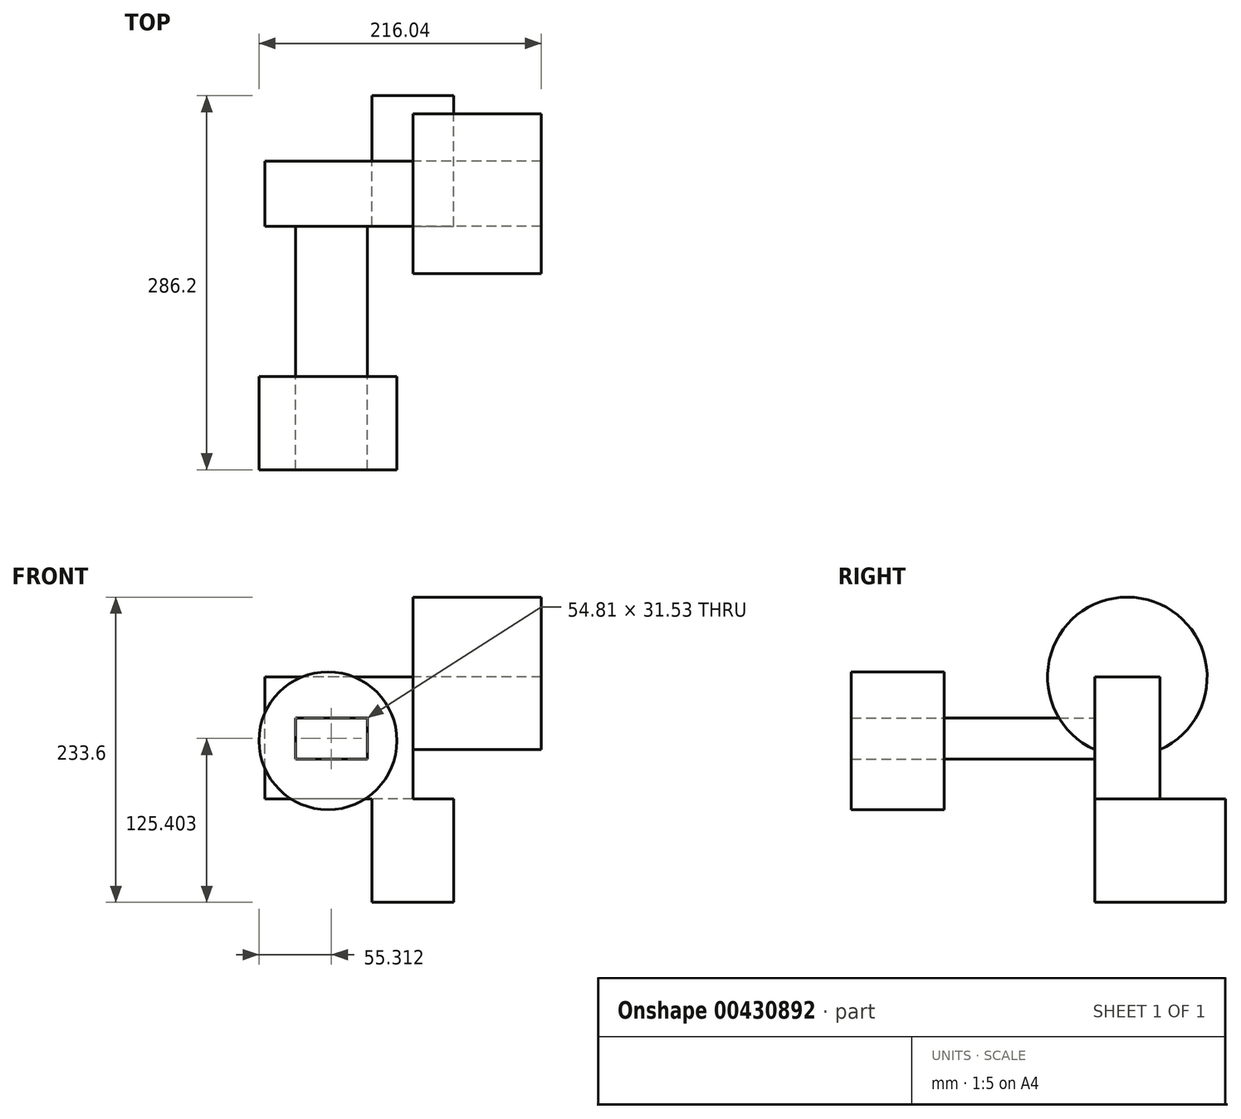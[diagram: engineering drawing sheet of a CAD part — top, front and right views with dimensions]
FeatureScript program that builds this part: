
annotation { "Feature Type Name" : "Feature", "Feature Type Description" : "" }
export const myFeature = defineFeature(function(context is Context, id is Id, definition is map)
    precondition{}
    {
        {
            var Q0;
            Q0=qCreatedBy(makeId("Front.planeOp"),FACE);
            var sketch = newSketch(context, id + "F0", { "sketchPlane" : qUnion([Q0])});
            skLineSegment(sketch, "E0.bottom", {"start": v(56.63, -46.67) * mm, "end": v(-56.63, -46.67) * mm});
            skLineSegment(sketch, "E0.top", {"start": v(56.63, 46.67) * mm, "end": v(-56.63, 46.67) * mm});
            skLineSegment(sketch, "E0.left", {"start": v(56.63, -46.67) * mm, "end": v(56.63, 46.67) * mm});
            skLineSegment(sketch, "E0.right", {"start": v(-56.63, -46.67) * mm, "end": v(-56.63, 46.67) * mm});
            skPoint(sketch, "E0.middle", {"position": v(0, 0) * mm});
            skSolve(sketch);
        }
        {
            var Q0;
            Q0=makeQuery(id+"F0.imprint","IMPRINT",FACE,{"disambiguationData":[TD([[makeQuery(id+"F0.imprint","IMPRINT",EDGE,{"derivedFrom":sQuery(id+"F0.wireOp",EDGE,"E0.bottom")}),-1.0]])]});
            extrude(context, id + "F1", {"entities" : qUnion([Q0]), "depth" : 25 * mm});
        }
        {
            var Q0;
            Q0=makeQuery(id+"F1.opExtrude","CAP_FACE",FACE,{"disambiguationData":[OSD([sQuery(id+"F0.wireOp",EDGE,"E0.bottom"),sQuery(id+"F0.wireOp",EDGE,"E0.top"),sQuery(id+"F0.wireOp",EDGE,"E0.left"),sQuery(id+"F0.wireOp",EDGE,"E0.right")])],"isStart":false});
            var sketch = newSketch(context, id + "F2", { "sketchPlane" : qUnion([Q0])});
            skLineSegment(sketch, "E1.bottom", {"start": v(21.62, -16.23) * mm, "end": v(-33.18, -16.23) * mm});
            skLineSegment(sketch, "E1.top", {"start": v(21.62, 15.3) * mm, "end": v(-33.18, 15.3) * mm});
            skLineSegment(sketch, "E1.left", {"start": v(21.62, -16.23) * mm, "end": v(21.62, 15.3) * mm});
            skLineSegment(sketch, "E1.right", {"start": v(-33.18, -16.23) * mm, "end": v(-33.18, 15.3) * mm});
            skSolve(sketch);
        }
        {
            var Q0;
            Q0=makeQuery(id+"F2.imprint","IMPRINT",FACE,{"disambiguationData":[TD([[makeQuery(id+"F2.imprint","IMPRINT",EDGE,{"derivedFrom":sQuery(id+"F2.wireOp",EDGE,"E1.bottom")}),-1.0]])]});
            extrude(context, id + "F3", {"entities" : qUnion([Q0]), "operationType" : NewBodyOperationType.ADD, "depth" : 115.04 * mm});
        }
        {
            var Q0;
            Q0=makeQuery(id+"F3.opExtrude","CAP_FACE",FACE,{"disambiguationData":[OSD([sQuery(id+"F2.wireOp",EDGE,"E1.bottom"),sQuery(id+"F2.wireOp",EDGE,"E1.top"),sQuery(id+"F2.wireOp",EDGE,"E1.left"),sQuery(id+"F2.wireOp",EDGE,"E1.right")])],"isStart":false});
            var sketch = newSketch(context, id + "F4", { "sketchPlane" : qUnion([Q0])});
            skSolve(sketch);
        }
        {
            var Q0;
            Q0=makeQuery(id+"F1.opExtrude","CAP_FACE",FACE,{"disambiguationData":[OSD([sQuery(id+"F0.wireOp",EDGE,"E0.bottom"),sQuery(id+"F0.wireOp",EDGE,"E0.top"),sQuery(id+"F0.wireOp",EDGE,"E0.left"),sQuery(id+"F0.wireOp",EDGE,"E0.right")])],"isStart":false});
            var Q1;
            Q1=makeQuery(id+"F4.imprint","IMPRINT",FACE,{"disambiguationData":[TD([[makeQuery(id+"F4.imprint","IMPRINT",EDGE,{"derivedFrom":makeQuery(id+"F3.opExtrude","CAP_EDGE",EDGE,{"disambiguationData":[OSD([sQuery(id+"F2.wireOp",EDGE,"E1.bottom")])],"isStart":false})}),-1.0]])]});
            extrude(context, id + "F5", {"entities" : qUnion([Q0, Q1]), "operationType" : NewBodyOperationType.ADD, "depth" : 25 * mm});
        }
        {
            var Q0;
            Q0=makeQuery(id+"F5.opExtrude","CAP_FACE",FACE,{"disambiguationData":[OSD([sQuery(id+"F2.wireOp",EDGE,"E1.bottom"),sQuery(id+"F2.wireOp",EDGE,"E1.top"),sQuery(id+"F2.wireOp",EDGE,"E1.left"),sQuery(id+"F2.wireOp",EDGE,"E1.right")])],"isStart":false});
            var sketch = newSketch(context, id + "F6", { "sketchPlane" : qUnion([Q0])});
            skCircle(sketch, "E2", {"center": v(-8.33, -2.19) * mm, "radius": 52.76 * mm});
            skSolve(sketch);
        }
        {
            var Q0;
            Q0=makeQuery(id+"F6.imprint","IMPRINT",FACE,{"disambiguationData":[TD([[makeQuery(id+"F6.imprint","IMPRINT",EDGE,{"derivedFrom":sQuery(id+"F6.wireOp",EDGE,"E2")}),1.0]])]});
            extrude(context, id + "F7", {"entities" : qUnion([Q0]), "depth" : 71.16 * mm});
        }
        {
            var Q0;
            {var subQ0=sQuery(id+"F0.wireOp",EDGE,"E0.bottom");Q0=makeQuery(id+"F5.boolean.opBoolean","MERGE",FACE,{"derivedFrom":[makeQuery(id+"F1.opExtrude","SWEPT_FACE",FACE,{"disambiguationData":[OSD([subQ0])]}),makeQuery(id+"F5.opExtrude","SWEPT_FACE",FACE,{"disambiguationData":[OSD([subQ0])]})]});}
            var sketch = newSketch(context, id + "F8", { "sketchPlane" : qUnion([Q0])});
            skLineSegment(sketch, "E3.bottom", {"start": v(25.33, 50) * mm, "end": v(87.93, 50) * mm});
            skLineSegment(sketch, "E3.top", {"start": v(25.33, -50) * mm, "end": v(87.93, -50) * mm});
            skLineSegment(sketch, "E3.left", {"start": v(25.33, 50) * mm, "end": v(25.33, -50) * mm});
            skLineSegment(sketch, "E3.right", {"start": v(87.93, 50) * mm, "end": v(87.93, -50) * mm});
            skPoint(sketch, "E3.middle", {"position": v(56.63, 0) * mm});
            skSolve(sketch);
        }
        {
            var Q0;
            Q0 = qSketchRegion(id + "F8", true);
            extrude(context, id + "F9", {"entities" : qUnion([Q0]), "operationType" : NewBodyOperationType.ADD, "depth" : 79.2 * mm});
        }
        {
            var Q0;
            Q0=makeQuery(id+"F9.boolean.opBoolean","MERGE",FACE,{"derivedFrom":[makeQuery(id+"F5.opExtrude","CAP_FACE",FACE,{"disambiguationData":[OSD([sQuery(id+"F0.wireOp",EDGE,"E0.bottom"),sQuery(id+"F0.wireOp",EDGE,"E0.top"),sQuery(id+"F0.wireOp",EDGE,"E0.left"),sQuery(id+"F0.wireOp",EDGE,"E0.right")])],"isStart":false}),makeQuery(id+"F9.opExtrude","SWEPT_FACE",FACE,{"disambiguationData":[OSD([sQuery(id+"F8.wireOp",EDGE,"E3.bottom")])]})]});
            var sketch = newSketch(context, id + "F10", { "sketchPlane" : qUnion([Q0])});
            skSolve(sketch);
        }
        {
            var Q0;
            Q0=makeQuery(id+"F10.imprint","IMPRINT",FACE,{"disambiguationData":[TD([[makeQuery(id+"F10.imprint","IMPRINT",EDGE,{"derivedFrom":makeQuery(id+"F5.opExtrude","CAP_EDGE",EDGE,{"disambiguationData":[OSD([sQuery(id+"F0.wireOp",EDGE,"E0.top")])],"isStart":false})}),1.0]])]});
            var sketch = newSketch(context, id + "F11", { "sketchPlane" : qUnion([Q0])});
            skEllipse(sketch, "E4", {"center": v(58.46, -81.77) * mm, "majorRadius": 30.53 * mm, "minorRadius": 60.92 * mm, "majorAxis": v(0, 1)});
            skSolve(sketch);
        }
        {
            var Q0;
            Q0=sQuery(id+"F11.wireOp",EDGE,"E4");
            extrude(context, id + "F12", {"bodyType" : ToolBodyType.SURFACE, "surfaceEntities" : qUnion([Q0]), "depth" : 120.61 * mm});
        }
        {
            var Q0;
            {var subQ0=sQuery(id+"F0.wireOp",EDGE,"E0.left");Q0=makeQuery(id+"F5.boolean.opBoolean","MERGE",FACE,{"derivedFrom":[makeQuery(id+"F1.opExtrude","SWEPT_FACE",FACE,{"disambiguationData":[OSD([subQ0])]}),makeQuery(id+"F5.opExtrude","SWEPT_FACE",FACE,{"disambiguationData":[OSD([subQ0])]})]});}
            var sketch = newSketch(context, id + "F13", { "sketchPlane" : qUnion([Q0])});
            skCircle(sketch, "E5", {"center": v(-25, 46.67) * mm, "radius": 61.05 * mm});
            skSolve(sketch);
        }
        {
            var Q0;
            {var subQ1=sQuery(id+"F0.wireOp",EDGE,"E0.left");var subQ6=sQuery(id+"F0.wireOp",EDGE,"E0.top");var subQ7=makeQuery(id+"F5.boolean.opBoolean","MERGE",EDGE,{"derivedFrom":[makeQuery(id+"F1.opExtrude","SWEPT_EDGE",EDGE,{"disambiguationData":[OSD([subQ6,subQ1])]}),makeQuery(id+"F5.opExtrude","SWEPT_EDGE",EDGE,{"disambiguationData":[OSD([subQ6,subQ1])]})]});Q0=makeQuery(id+"F13.imprint","IMPRINT",FACE,{"disambiguationData":[TD([[makeQuery(id+"F13.imprint","IMPRINT",EDGE,{"derivedFrom":subQ7}),1.0]])]});}
            extrude(context, id + "F14", {"entities" : qUnion([Q0]), "depth" : 98.32 * mm});
        }
    });
